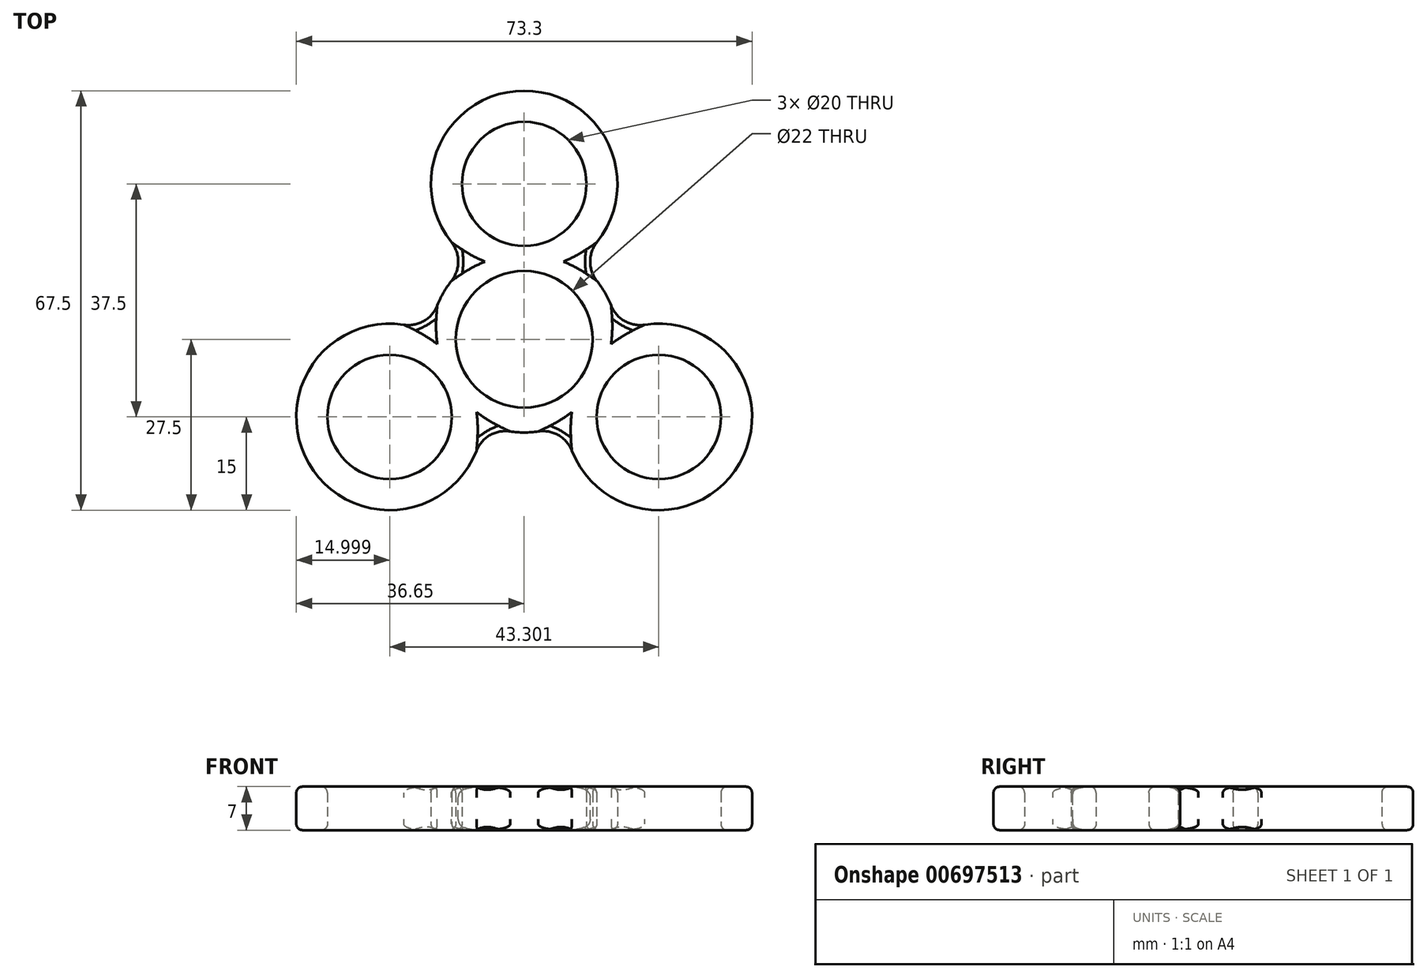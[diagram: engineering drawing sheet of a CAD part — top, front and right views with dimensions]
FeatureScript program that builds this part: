
annotation { "Feature Type Name" : "Feature", "Feature Type Description" : "" }
export const myFeature = defineFeature(function(context is Context, id is Id, definition is map)
    precondition{}
    {
        {
            var Q0;
            Q0=qCreatedBy(makeId("Top.planeOp"),FACE);
            var sketch = newSketch(context, id + "F0", { "sketchPlane" : qUnion([Q0])});
            skCircle(sketch, "E0", {"center": v(0, 0) * mm, "radius": 11 * mm});
            skArc(sketch, "E1", {"start": v(-8.3, 12.5) * mm, "mid": v(-13, 7.5) * mm, "end": v(-14.97, 0.93) * mm});
            skLineSegment(sketch, "E2", {"start": v(0, 0) * mm, "end": v(0, 25) * mm});
            skCircle(sketch, "E3", {"center": v(0, 25) * mm, "radius": 10 * mm});
            skCircle(sketch, "E4.1.0", {"center": v(-21.65, -12.5) * mm, "radius": 10 * mm});
            skArc(sketch, "E4.1.1", {"start": v(-14.97, 0.93) * mm, "mid": v(-34.64, -20) * mm, "end": v(-6.68, -13.43) * mm});
            skCircle(sketch, "E4.2.0", {"center": v(21.65, -12.5) * mm, "radius": 10 * mm});
            skArc(sketch, "E4.2.1", {"start": v(6.68, -13.43) * mm, "mid": v(34.64, -20) * mm, "end": v(14.97, 0.93) * mm});
            skArc(sketch, "E5.trimOffspring", {"start": v(8.3, 12.5) * mm, "mid": v(0, 40) * mm, "end": v(-8.3, 12.5) * mm});
            skArc(sketch, "E6.trimOffspring", {"start": v(-6.68, -13.43) * mm, "mid": v(0, -15) * mm, "end": v(6.68, -13.43) * mm});
            skArc(sketch, "E7.trimOffspring", {"start": v(14.97, 0.93) * mm, "mid": v(13, 7.5) * mm, "end": v(8.3, 12.5) * mm});
            skSolve(sketch);
        }
        {
            var Q0;
            Q0=makeQuery(id+"F0.imprint","IMPRINT",FACE,{"disambiguationData":[TD([[makeQuery(id+"F0.imprint","IMPRINT",EDGE,{"derivedFrom":sQuery(id+"F0.wireOp",EDGE,"E0")}),-1.0]])]});
            extrude(context, id + "F1", {"entities" : qUnion([Q0]), "depth" : 7 * mm, "offsetDistance" : 25 * mm});
        }
        {
            var Q0;
            Q0=makeQuery(id+"F1.opExtrude","CAP_EDGE",EDGE,{"disambiguationData":[OSD([sQuery(id+"F0.wireOp",EDGE,"E4.1.0")])],"isStart":false});
            var Q1;
            Q1=makeQuery(id+"F1.opExtrude","CAP_EDGE",EDGE,{"disambiguationData":[OSD([sQuery(id+"F0.wireOp",EDGE,"E0")])],"isStart":false});
            var Q2;
            Q2=makeQuery(id+"F1.opExtrude","CAP_EDGE",EDGE,{"disambiguationData":[OSD([sQuery(id+"F0.wireOp",EDGE,"E3")])],"isStart":false});
            var Q3;
            Q3=makeQuery(id+"F1.opExtrude","CAP_EDGE",EDGE,{"disambiguationData":[OSD([sQuery(id+"F0.wireOp",EDGE,"E4.2.0")])],"isStart":false});
            var Q4;
            Q4=makeQuery(id+"F1.opExtrude","CAP_EDGE",EDGE,{"disambiguationData":[OSD([sQuery(id+"F0.wireOp",EDGE,"E4.2.0")])],"isStart":true});
            var Q5;
            Q5=makeQuery(id+"F1.opExtrude","CAP_EDGE",EDGE,{"disambiguationData":[OSD([sQuery(id+"F0.wireOp",EDGE,"E0")])],"isStart":true});
            var Q6;
            Q6=makeQuery(id+"F1.opExtrude","CAP_EDGE",EDGE,{"disambiguationData":[OSD([sQuery(id+"F0.wireOp",EDGE,"E3")])],"isStart":true});
            var Q7;
            Q7=makeQuery(id+"F1.opExtrude","CAP_EDGE",EDGE,{"disambiguationData":[OSD([sQuery(id+"F0.wireOp",EDGE,"E4.1.0")])],"isStart":true});
            var Q8;
            Q8=makeQuery(id+"F1.opExtrude","CAP_EDGE",EDGE,{"disambiguationData":[OSD([sQuery(id+"F0.wireOp",EDGE,"E4.2.1")])],"isStart":false});
            var Q9;
            Q9=makeQuery(id+"F1.opExtrude","CAP_EDGE",EDGE,{"disambiguationData":[OSD([sQuery(id+"F0.wireOp",EDGE,"E4.2.1")])],"isStart":true});
            var Q10;
            Q10=makeQuery(id+"F1.opExtrude","CAP_EDGE",EDGE,{"disambiguationData":[OSD([sQuery(id+"F0.wireOp",EDGE,"E7.trimOffspring")])],"isStart":false});
            var Q11;
            Q11=makeQuery(id+"F1.opExtrude","CAP_EDGE",EDGE,{"disambiguationData":[OSD([sQuery(id+"F0.wireOp",EDGE,"E7.trimOffspring")])],"isStart":true});
            var Q12;
            Q12=makeQuery(id+"F1.opExtrude","CAP_EDGE",EDGE,{"disambiguationData":[OSD([sQuery(id+"F0.wireOp",EDGE,"E5.trimOffspring")])],"isStart":false});
            var Q13;
            Q13=makeQuery(id+"F1.opExtrude","CAP_EDGE",EDGE,{"disambiguationData":[OSD([sQuery(id+"F0.wireOp",EDGE,"E1")])],"isStart":true});
            var Q14;
            Q14=makeQuery(id+"F1.opExtrude","CAP_EDGE",EDGE,{"disambiguationData":[OSD([sQuery(id+"F0.wireOp",EDGE,"E5.trimOffspring")])],"isStart":true});
            var Q15;
            Q15=makeQuery(id+"F1.opExtrude","CAP_EDGE",EDGE,{"disambiguationData":[OSD([sQuery(id+"F0.wireOp",EDGE,"E4.1.1")])],"isStart":false});
            var Q16;
            Q16=makeQuery(id+"F1.opExtrude","CAP_EDGE",EDGE,{"disambiguationData":[OSD([sQuery(id+"F0.wireOp",EDGE,"E6.trimOffspring")])],"isStart":false});
            var Q17;
            Q17=makeQuery(id+"F1.opExtrude","CAP_EDGE",EDGE,{"disambiguationData":[OSD([sQuery(id+"F0.wireOp",EDGE,"E6.trimOffspring")])],"isStart":true});
            var Q18;
            Q18=makeQuery(id+"F1.opExtrude","CAP_EDGE",EDGE,{"disambiguationData":[OSD([sQuery(id+"F0.wireOp",EDGE,"E1")])],"isStart":false});
            fillet(context, id + "F2", {"entities" : qUnion([Q0, Q1, Q2, Q3, Q4, Q5, Q6, Q7, Q8, Q9, Q10, Q11, Q12, Q13, Q14, Q15, Q16, Q17, Q18]), "radius" : 1 * mm, "tangentPropagation" : true, "allowEdgeOverflow" : false});
        }
        {
            var Q0;
            Q0=makeQuery(id+"F1.opExtrude","CAP_EDGE",EDGE,{"disambiguationData":[OSD([sQuery(id+"F0.wireOp",EDGE,"E4.1.1")])],"isStart":true});
            fillet(context, id + "F3", {"entities" : qUnion([Q0]), "radius" : 1 * mm, "tangentPropagation" : true, "allowEdgeOverflow" : false});
        }
        {
            var Q0;
            Q0=makeQuery(id+"F1.opExtrude","SWEPT_EDGE",EDGE,{"disambiguationData":[OSD([sQuery(id+"F0.wireOp",EDGE,"E4.2.1"),sQuery(id+"F0.wireOp",EDGE,"E7.trimOffspring")])]});
            var Q1;
            Q1=makeQuery(id+"F1.opExtrude","SWEPT_EDGE",EDGE,{"disambiguationData":[OSD([sQuery(id+"F0.wireOp",EDGE,"E5.trimOffspring"),sQuery(id+"F0.wireOp",EDGE,"E7.trimOffspring")])]});
            var Q2;
            Q2=makeQuery(id+"F1.opExtrude","SWEPT_EDGE",EDGE,{"disambiguationData":[OSD([sQuery(id+"F0.wireOp",EDGE,"E1"),sQuery(id+"F0.wireOp",EDGE,"E4.1.1")])]});
            var Q3;
            Q3=makeQuery(id+"F1.opExtrude","SWEPT_EDGE",EDGE,{"disambiguationData":[OSD([sQuery(id+"F0.wireOp",EDGE,"E1"),sQuery(id+"F0.wireOp",EDGE,"E5.trimOffspring")])]});
            var Q4;
            Q4=makeQuery(id+"F1.opExtrude","SWEPT_EDGE",EDGE,{"disambiguationData":[OSD([sQuery(id+"F0.wireOp",EDGE,"E4.1.1"),sQuery(id+"F0.wireOp",EDGE,"E6.trimOffspring")])]});
            var Q5;
            Q5=makeQuery(id+"F1.opExtrude","SWEPT_EDGE",EDGE,{"disambiguationData":[OSD([sQuery(id+"F0.wireOp",EDGE,"E4.2.1"),sQuery(id+"F0.wireOp",EDGE,"E6.trimOffspring")])]});
            fillet(context, id + "F4", {"entities" : qUnion([Q0, Q1, Q2, Q3, Q4, Q5]), "radius" : 5 * mm, "tangentPropagation" : true, "allowEdgeOverflow" : false});
        }
    });
